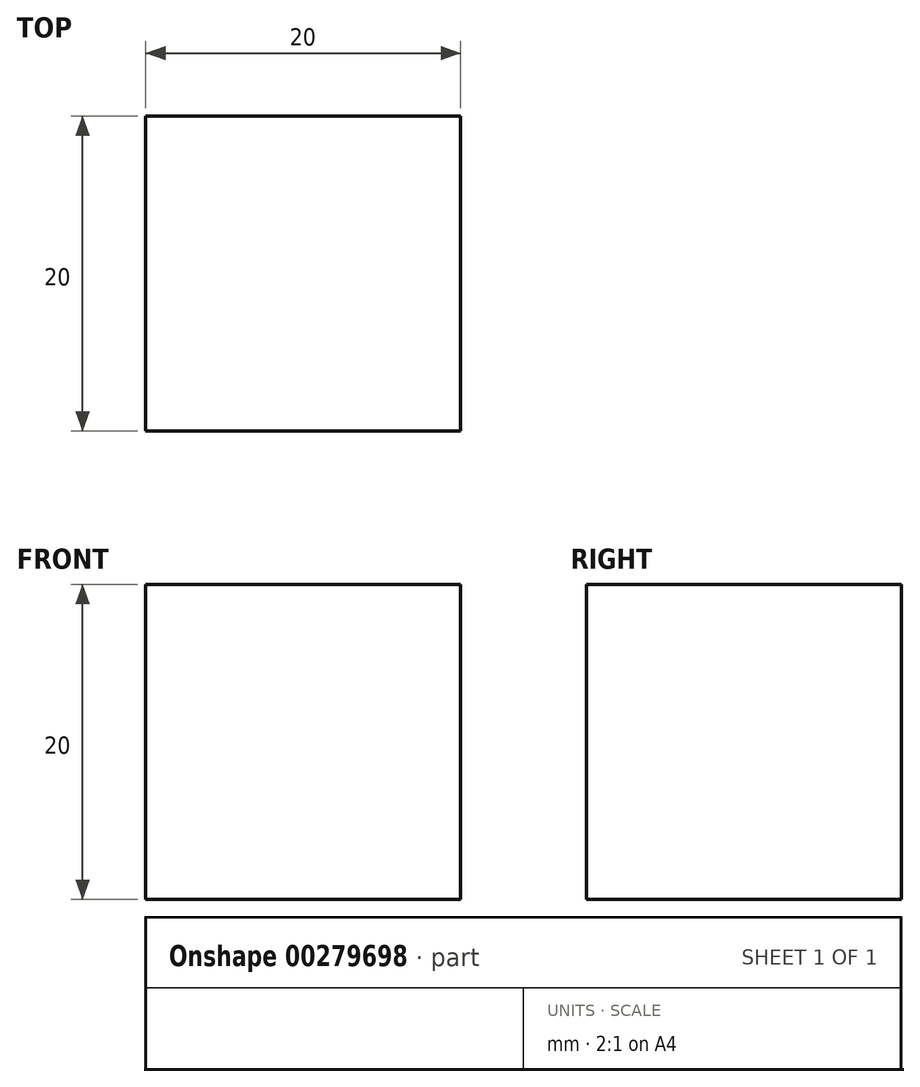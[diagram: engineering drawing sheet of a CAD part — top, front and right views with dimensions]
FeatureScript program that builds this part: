
annotation { "Feature Type Name" : "Feature", "Feature Type Description" : "" }
export const myFeature = defineFeature(function(context is Context, id is Id, definition is map)
    precondition{}
    {
        {
            var Q0;
            Q0=qCreatedBy(makeId("Front.planeOp"),FACE);
            var sketch = newSketch(context, id + "F0", { "sketchPlane" : qUnion([Q0])});
            skLineSegment(sketch, "E0.bottom", {"start": v(0, 0) * mm, "end": v(20, 0) * mm});
            skLineSegment(sketch, "E0.top", {"start": v(0, 20) * mm, "end": v(20, 20) * mm});
            skLineSegment(sketch, "E0.left", {"start": v(0, 0) * mm, "end": v(0, 20) * mm});
            skLineSegment(sketch, "E0.right", {"start": v(20, 0) * mm, "end": v(20, 20) * mm});
            skSolve(sketch);
        }
        {
            var Q0;
            Q0 = qSketchRegion(id + "F0", true);
            extrude(context, id + "F1", {"entities" : qUnion([Q0]), "depth" : 20 * mm});
        }
    });
